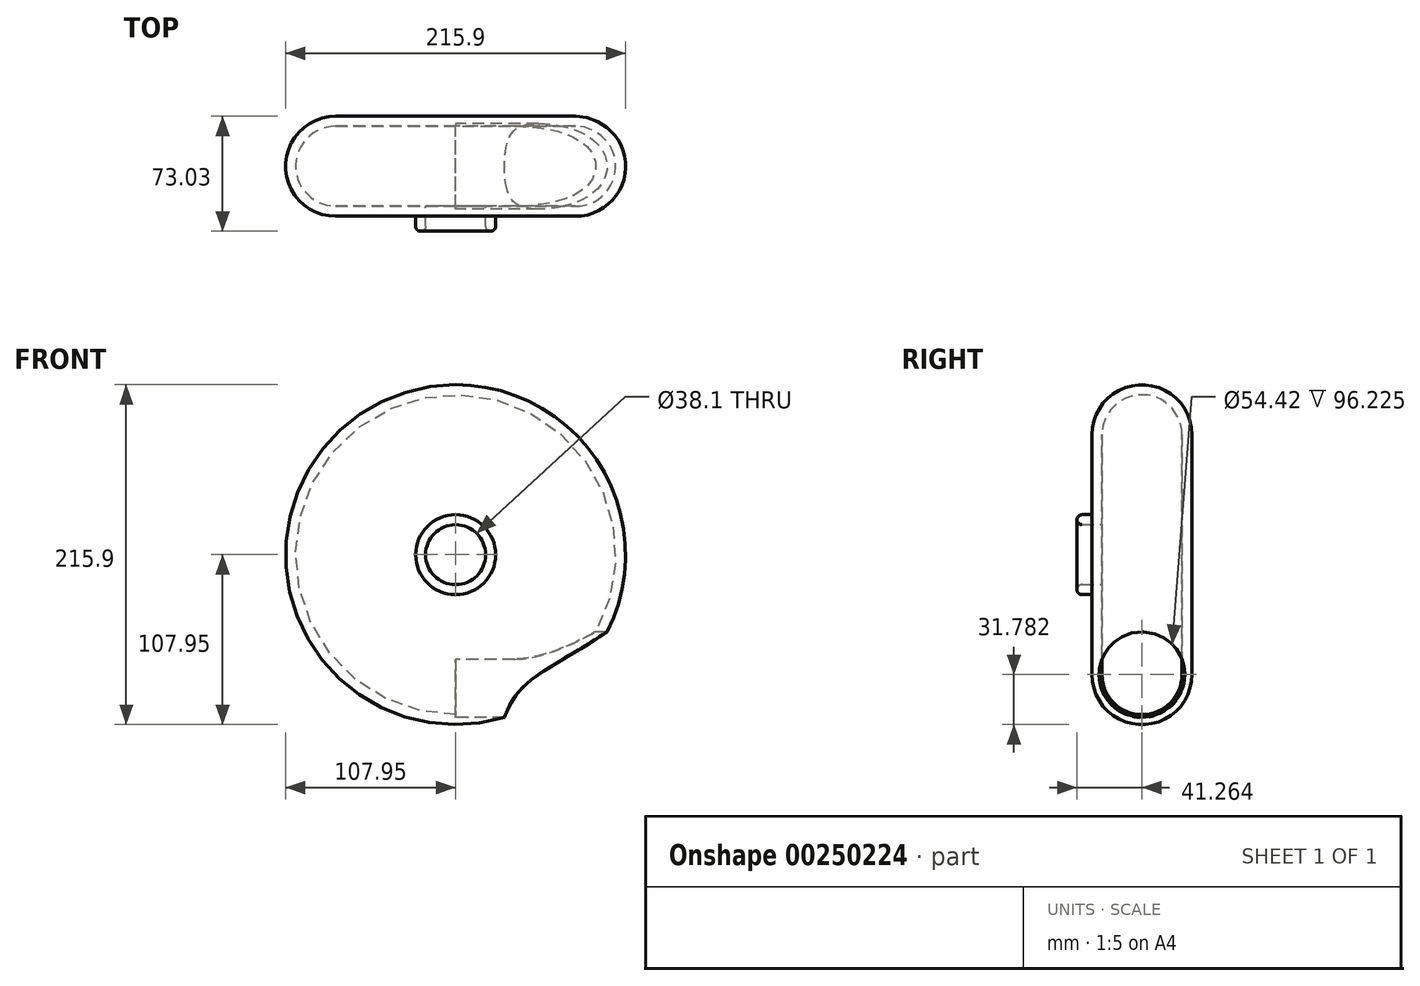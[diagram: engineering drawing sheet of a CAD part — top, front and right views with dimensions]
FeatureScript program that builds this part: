
annotation { "Feature Type Name" : "Feature", "Feature Type Description" : "" }
export const myFeature = defineFeature(function(context is Context, id is Id, definition is map)
    precondition{}
    {
        {
            var Q0;
            Q0=qCreatedBy(makeId("Top.planeOp"),FACE);
            var sketch = newSketch(context, id + "F0", { "sketchPlane" : qUnion([Q0])});
            skLineSegment(sketch, "E0", {"start": v(0, 0) * mm, "end": v(76.2, 0) * mm});
            skLineSegment(sketch, "E1", {"start": v(0, 0) * mm, "end": v(0, -6.35) * mm});
            skLineSegment(sketch, "E2", {"start": v(0, -6.35) * mm, "end": v(0, -57.15) * mm});
            skLineSegment(sketch, "E3", {"start": v(0, -57.15) * mm, "end": v(0, -63.5) * mm});
            skLineSegment(sketch, "E4", {"start": v(0, -63.5) * mm, "end": v(76.2, -63.5) * mm});
            skLineSegment(sketch, "E5", {"start": v(76.2, 0) * mm, "end": v(76.2, -63.5) * mm});
            skArc(sketch, "E6", {"start": v(76.2, -63.5) * mm, "mid": v(107.95, -31.75) * mm, "end": v(76.2, 0) * mm});
            skLineSegment(sketch, "E7", {"start": v(0, -6.35) * mm, "end": v(76.2, -6.35) * mm});
            skLineSegment(sketch, "E8", {"start": v(0, -57.15) * mm, "end": v(76.2, -57.15) * mm});
            skArc(sketch, "E9", {"start": v(76.2, -57.15) * mm, "mid": v(101.6, -31.75) * mm, "end": v(76.2, -6.35) * mm});
            skLineSegment(sketch, "E10", {"start": v(0, -63.5) * mm, "end": v(25.4, -63.5) * mm});
            skLineSegment(sketch, "E11", {"start": v(25.4, -63.5) * mm, "end": v(25.4, -69.85) * mm});
            skLineSegment(sketch, "E12", {"start": v(25.4, -63.5) * mm, "end": v(19.05, -63.5) * mm});
            skLineSegment(sketch, "E13", {"start": v(19.05, -63.5) * mm, "end": v(19.05, -69.85) * mm});
            skLineSegment(sketch, "E14", {"start": v(19.05, -69.85) * mm, "end": v(25.4, -69.85) * mm});
            skArc(sketch, "E15", {"start": v(25.4, -69.85) * mm, "mid": v(22.23, -73.02) * mm, "end": v(19.05, -69.85) * mm});
            skLineSegment(sketch, "E16", {"start": v(19.05, -63.5) * mm, "end": v(19.05, -57.15) * mm});
            skLineSegment(sketch, "E17", {"start": v(25.4, -69.85) * mm, "end": v(25.4, -76.2) * mm});
            skArc(sketch, "E18", {"start": v(19.05, -69.85) * mm, "mid": v(20.9, -74.34) * mm, "end": v(25.4, -76.2) * mm});
            skSolve(sketch);
        }
        {
            var Q0;
            {var subQ0=sQuery(id+"F0.wireOp",EDGE,"E0");Q0=makeQuery(id+"F0.imprint","IMPRINT",FACE,{"disambiguationData":[TD([[makeQuery(id+"F0.imprint","IMPRINT",EDGE,{"derivedFrom":subQ0}),-1.0]])]});}
            var Q1;
            {var subQ0=sQuery(id+"F0.wireOp",EDGE,"E6");Q1=makeQuery(id+"F0.imprint","IMPRINT",FACE,{"disambiguationData":[TD([[makeQuery(id+"F0.imprint","IMPRINT",EDGE,{"derivedFrom":subQ0}),1.0]])]});}
            var Q2;
            {var subQ4=sQuery(id+"F0.wireOp",EDGE,"E4");Q2=makeQuery(id+"F0.imprint","IMPRINT",FACE,{"disambiguationData":[TD([[makeQuery(id+"F0.imprint","IMPRINT",EDGE,{"derivedFrom":subQ4}),1.0]])]});}
            var Q3;
            Q3=makeQuery(id+"F0.imprint","IMPRINT",FACE,{"disambiguationData":[TD([[makeQuery(id+"F0.imprint","IMPRINT",EDGE,{"derivedFrom":sQuery(id+"F0.wireOp",EDGE,"E11")}),-1.0]])]});
            var Q4;
            Q4=makeQuery(id+"F0.imprint","IMPRINT",FACE,{"disambiguationData":[TD([[makeQuery(id+"F0.imprint","IMPRINT",EDGE,{"derivedFrom":sQuery(id+"F0.wireOp",EDGE,"E14")}),-1.0]])]});
            var Q5;
            Q5=makeQuery(id+"F0.imprint","IMPRINT",FACE,{"disambiguationData":[TD([[makeQuery(id+"F0.imprint","IMPRINT",EDGE,{"derivedFrom":sQuery(id+"F0.wireOp",EDGE,"E15")}),1.0]])]});
            var Q6;
            Q6=sQuery(id+"F0.wireOp",EDGE,"E2");
            revolve(context, id + "F1", {"entities" : qUnion([Q0, Q1, Q2, Q3, Q4, Q5]), "axis" : qUnion([Q6]), "revolveType" : RevolveType.FULL});
        }
        {
            var Q0;
            Q0=qCreatedBy(makeId("Right.planeOp"),FACE);
            var sketch = newSketch(context, id + "F2", { "sketchPlane" : qUnion([Q0])});
            skLineSegment(sketch, "E19", {"start": v(-76.44, -76.17) * mm, "end": v(0, -76.17) * mm});
            skLineSegment(sketch, "E20", {"start": v(0, -76.17) * mm, "end": v(-63.53, -76.17) * mm});
            skCircle(sketch, "E21", {"center": v(-31.77, -76.17) * mm, "radius": 27.2 * mm});
            skSolve(sketch);
        }
        {
            var Q0;
            Q0 = qSketchRegion(id + "F2", true);
            extrude(context, id + "F3", {"entities" : qUnion([Q0]), "operationType" : NewBodyOperationType.REMOVE, "depth" : 101.6 * mm});
        }
    });
